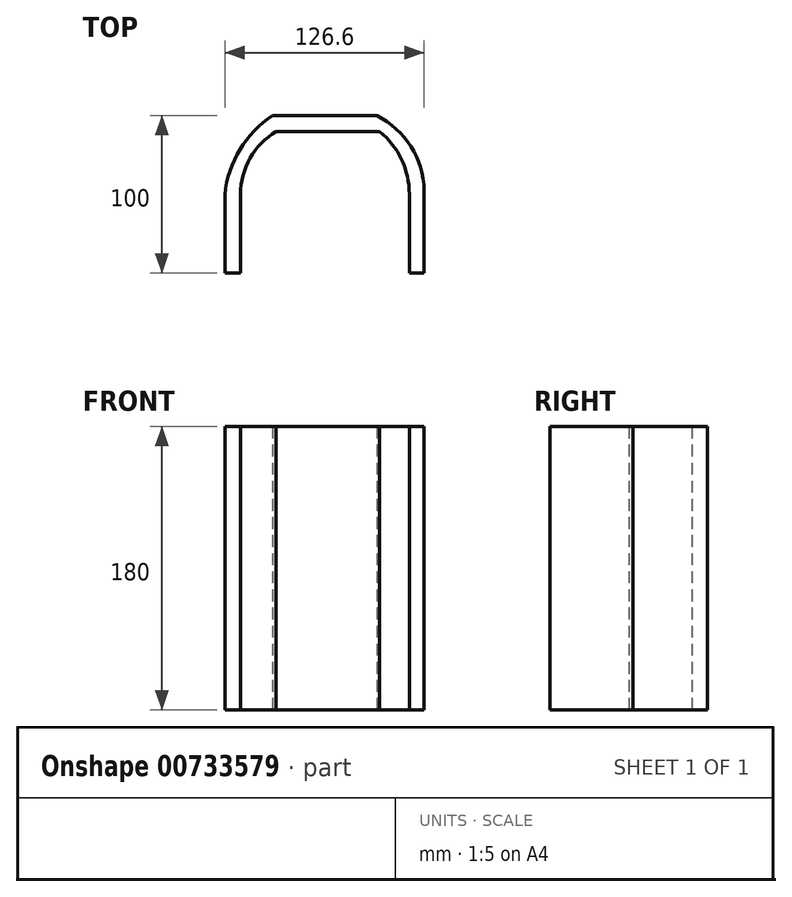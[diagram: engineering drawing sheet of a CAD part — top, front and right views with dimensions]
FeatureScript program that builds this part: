
annotation { "Feature Type Name" : "Feature", "Feature Type Description" : "" }
export const myFeature = defineFeature(function(context is Context, id is Id, definition is map)
    precondition{}
    {
        {
            var Q0;
            Q0=qCreatedBy(makeId("Top.planeOp"),FACE);
            var sketch = newSketch(context, id + "F0", { "sketchPlane" : qUnion([Q0])});
            skLineSegment(sketch, "E0.bottom", {"start": v(63.3, -50) * mm, "end": v(53.88, -50) * mm});
            skLineSegment(sketch, "E0.top", {"start": v(33.32, 50) * mm, "end": v(-33.06, 50) * mm});
            skLineSegment(sketch, "E0.left", {"start": v(63.3, -50) * mm, "end": v(63.3, 2.56) * mm});
            skLineSegment(sketch, "E0.right", {"start": v(-63.3, -50) * mm, "end": v(-63.3, 0) * mm});
            skPoint(sketch, "E0.middle", {"position": v(0, 0) * mm});
            skArc(sketch, "E1", {"start": v(-33.06, 50) * mm, "mid": v(-53.69, 28.33) * mm, "end": v(-63.3, 0) * mm});
            skArc(sketch, "E2", {"start": v(63.3, 0) * mm, "mid": v(55.54, 29.34) * mm, "end": v(33.32, 50) * mm});
            skLineSegment(sketch, "E3", {"start": v(-53.3, -50) * mm, "end": v(-53.3, 0) * mm});
            skLineSegment(sketch, "E4", {"start": v(53.88, -50) * mm, "end": v(53.88, 0) * mm});
            skLineSegment(sketch, "E5", {"start": v(-30.64, 39.94) * mm, "end": v(35.02, 39.94) * mm});
            skArc(sketch, "E6", {"start": v(-30.64, 39.94) * mm, "mid": v(-47.24, 22.96) * mm, "end": v(-53.3, 0) * mm});
            skArc(sketch, "E7", {"start": v(53.88, 0) * mm, "mid": v(48.93, 22.09) * mm, "end": v(35.02, 39.94) * mm});
            skPoint(sketch, "E8.orphan", {"position": v(-63.3, 50) * mm});
            skPoint(sketch, "E9.orphan", {"position": v(63.3, 50) * mm});
            skLineSegment(sketch, "E10.trimOffspring", {"start": v(-53.3, -50) * mm, "end": v(-63.3, -50) * mm});
            skSolve(sketch);
        }
        {
            var Q0;
            {var subQ4=sQuery(id+"F0.wireOp",EDGE,"E0.bottom");Q0=makeQuery(id+"F0.imprint","IMPRINT",FACE,{"disambiguationData":[TD([[makeQuery(id+"F0.imprint","IMPRINT",EDGE,{"derivedFrom":subQ4}),-1.0]])]});}
            extrude(context, id + "F1", {"entities" : qUnion([Q0]), "depth" : 180 * mm, "offsetDistance" : 25 * mm});
        }
    });
